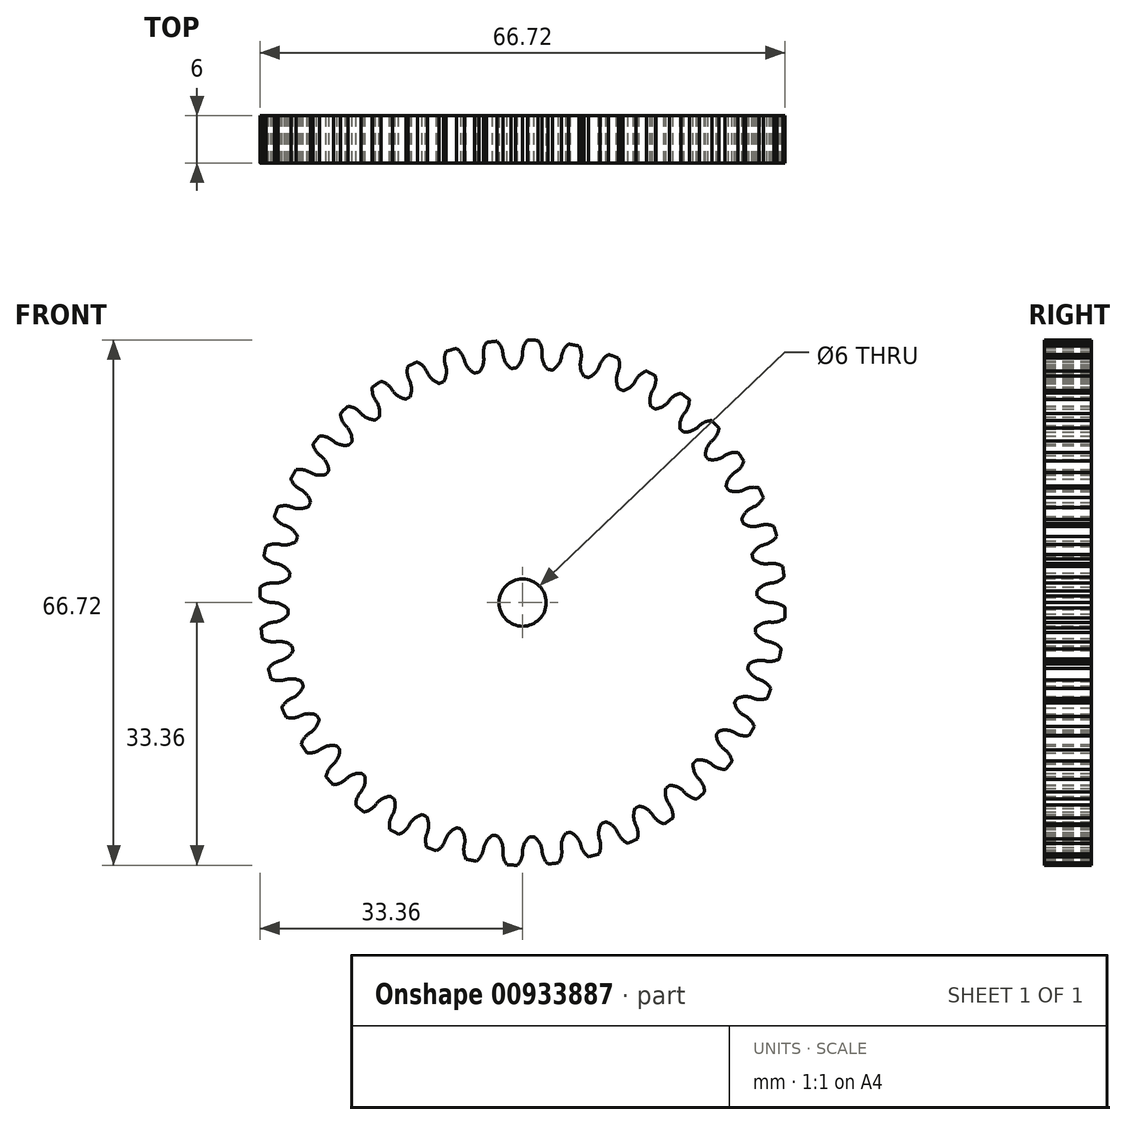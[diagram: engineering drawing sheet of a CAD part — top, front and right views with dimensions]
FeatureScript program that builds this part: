
annotation { "Feature Type Name" : "Feature", "Feature Type Description" : "" }
export const myFeature = defineFeature(function(context is Context, id is Id, definition is map)
    precondition{}
    {
        {
            var Q0;
            Q0=qCreatedBy(makeId("Front.planeOp"),FACE);
            var sketch = newSketch(context, id + "F0", { "sketchPlane" : qUnion([Q0])});
            skCircle(sketch, "E0", {"center": v(0, 0) * mm, "radius": 29.8 * mm});
            skArc(sketch, "E1", {"start": v(1.97, 33.31) * mm, "mid": v(1.31, 33.34) * mm, "end": v(0.65, 33.36) * mm});
            skArc(sketch, "E2", {"start": v(2.48, 31.49) * mm, "mid": v(2.4, 32.45) * mm, "end": v(1.97, 33.31) * mm});
            skArc(sketch, "E3", {"start": v(2.48, 31.49) * mm, "mid": v(2.65, 30.48) * mm, "end": v(3.21, 29.62) * mm});
            skArc(sketch, "E4", {"start": v(-0.88, 29.78) * mm, "mid": v(-0.2, 30.68) * mm, "end": v(0, 31.78) * mm});
            skArc(sketch, "E5.trimOffspring", {"start": v(0.65, 33.36) * mm, "mid": v(0.18, 32.63) * mm, "end": v(0, 31.78) * mm});
            skArc(sketch, "E6.1.0", {"start": v(-3.26, 33.2) * mm, "mid": v(-3.92, 33.14) * mm, "end": v(-4.58, 33.05) * mm});
            skArc(sketch, "E6.1.1", {"start": v(-4.58, 33.05) * mm, "mid": v(-4.92, 32.26) * mm, "end": v(-4.97, 31.39) * mm});
            skArc(sketch, "E6.1.2", {"start": v(-2.48, 31.49) * mm, "mid": v(-2.7, 32.43) * mm, "end": v(-3.26, 33.2) * mm});
            skArc(sketch, "E6.1.3", {"start": v(-2.48, 31.49) * mm, "mid": v(-2.15, 30.52) * mm, "end": v(-1.46, 29.76) * mm});
            skArc(sketch, "E6.1.4", {"start": v(-5.52, 29.28) * mm, "mid": v(-5, 30.27) * mm, "end": v(-4.97, 31.39) * mm});
            skArc(sketch, "E6.2.0", {"start": v(-8.42, 32.3) * mm, "mid": v(-9.06, 32.12) * mm, "end": v(-9.7, 31.93) * mm});
            skArc(sketch, "E6.2.1", {"start": v(-9.7, 31.93) * mm, "mid": v(-9.9, 31.09) * mm, "end": v(-9.82, 30.22) * mm});
            skArc(sketch, "E6.2.2", {"start": v(-7.37, 30.71) * mm, "mid": v(-7.74, 31.6) * mm, "end": v(-8.42, 32.3) * mm});
            skArc(sketch, "E6.2.3", {"start": v(-7.37, 30.71) * mm, "mid": v(-6.9, 29.8) * mm, "end": v(-6.1, 29.16) * mm});
            skArc(sketch, "E6.2.4", {"start": v(-10.04, 28.05) * mm, "mid": v(-9.68, 29.11) * mm, "end": v(-9.82, 30.22) * mm});
            skArc(sketch, "E6.3.0", {"start": v(-13.36, 30.58) * mm, "mid": v(-13.97, 30.3) * mm, "end": v(-14.57, 30.02) * mm});
            skArc(sketch, "E6.3.1", {"start": v(-14.57, 30.02) * mm, "mid": v(-14.65, 29.16) * mm, "end": v(-14.43, 28.32) * mm});
            skArc(sketch, "E6.3.2", {"start": v(-12.08, 29.18) * mm, "mid": v(-12.59, 30) * mm, "end": v(-13.36, 30.58) * mm});
            skArc(sketch, "E6.3.3", {"start": v(-12.08, 29.18) * mm, "mid": v(-11.47, 28.36) * mm, "end": v(-10.59, 27.85) * mm});
            skArc(sketch, "E6.3.4", {"start": v(-14.3, 26.14) * mm, "mid": v(-14.11, 27.24) * mm, "end": v(-14.43, 28.32) * mm});
            skArc(sketch, "E6.4.0", {"start": v(-17.98, 28.1) * mm, "mid": v(-18.54, 27.75) * mm, "end": v(-19.09, 27.37) * mm});
            skArc(sketch, "E6.4.1", {"start": v(-19.09, 27.37) * mm, "mid": v(-19.03, 26.5) * mm, "end": v(-18.68, 25.71) * mm});
            skArc(sketch, "E6.4.2", {"start": v(-16.5, 26.93) * mm, "mid": v(-17.13, 27.67) * mm, "end": v(-17.98, 28.1) * mm});
            skArc(sketch, "E6.4.3", {"start": v(-16.5, 26.93) * mm, "mid": v(-15.77, 26.21) * mm, "end": v(-14.81, 25.85) * mm});
            skArc(sketch, "E6.4.4", {"start": v(-18.21, 23.58) * mm, "mid": v(-18.2, 24.7) * mm, "end": v(-18.68, 25.71) * mm});
            skArc(sketch, "E6.5.0", {"start": v(-22.16, 24.95) * mm, "mid": v(-22.65, 24.5) * mm, "end": v(-23.13, 24.05) * mm});
            skArc(sketch, "E6.5.1", {"start": v(-23.13, 24.05) * mm, "mid": v(-22.94, 23.2) * mm, "end": v(-22.47, 22.47) * mm});
            skArc(sketch, "E6.5.2", {"start": v(-20.51, 24.02) * mm, "mid": v(-21.24, 24.65) * mm, "end": v(-22.16, 24.95) * mm});
            skArc(sketch, "E6.5.3", {"start": v(-20.51, 24.02) * mm, "mid": v(-19.68, 23.42) * mm, "end": v(-18.67, 23.22) * mm});
            skArc(sketch, "E6.5.4", {"start": v(-21.68, 20.44) * mm, "mid": v(-21.84, 21.55) * mm, "end": v(-22.47, 22.47) * mm});
            skArc(sketch, "E6.6.0", {"start": v(-25.79, 21.18) * mm, "mid": v(-26.2, 20.66) * mm, "end": v(-26.6, 20.13) * mm});
            skArc(sketch, "E6.6.1", {"start": v(-26.6, 20.13) * mm, "mid": v(-26.29, 19.33) * mm, "end": v(-25.71, 18.68) * mm});
            skArc(sketch, "E6.6.2", {"start": v(-24.02, 20.51) * mm, "mid": v(-24.84, 21.02) * mm, "end": v(-25.79, 21.18) * mm});
            skArc(sketch, "E6.6.3", {"start": v(-24.02, 20.51) * mm, "mid": v(-23.1, 20.06) * mm, "end": v(-22.08, 20) * mm});
            skArc(sketch, "E6.6.4", {"start": v(-24.6, 16.8) * mm, "mid": v(-24.94, 17.87) * mm, "end": v(-25.71, 18.68) * mm});
            skArc(sketch, "E6.7.0", {"start": v(-28.78, 16.88) * mm, "mid": v(-29.11, 16.3) * mm, "end": v(-29.43, 15.72) * mm});
            skArc(sketch, "E6.7.1", {"start": v(-29.43, 15.72) * mm, "mid": v(-28.99, 14.98) * mm, "end": v(-28.32, 14.43) * mm});
            skArc(sketch, "E6.7.2", {"start": v(-26.93, 16.5) * mm, "mid": v(-27.82, 16.88) * mm, "end": v(-28.78, 16.88) * mm});
            skArc(sketch, "E6.7.3", {"start": v(-26.93, 16.5) * mm, "mid": v(-25.95, 16.2) * mm, "end": v(-24.93, 16.3) * mm});
            skArc(sketch, "E6.7.4", {"start": v(-26.93, 12.74) * mm, "mid": v(-27.43, 13.74) * mm, "end": v(-28.32, 14.43) * mm});
            skArc(sketch, "E6.8.0", {"start": v(-31.07, 12.17) * mm, "mid": v(-31.3, 11.55) * mm, "end": v(-31.53, 10.93) * mm});
            skArc(sketch, "E6.8.1", {"start": v(-31.53, 10.93) * mm, "mid": v(-30.97, 10.26) * mm, "end": v(-30.22, 9.82) * mm});
            skArc(sketch, "E6.8.2", {"start": v(-29.18, 12.09) * mm, "mid": v(-30.12, 12.32) * mm, "end": v(-31.07, 12.17) * mm});
            skArc(sketch, "E6.8.3", {"start": v(-29.18, 12.09) * mm, "mid": v(-28.17, 11.94) * mm, "end": v(-27.18, 12.2) * mm});
            skArc(sketch, "E6.8.4", {"start": v(-28.6, 8.37) * mm, "mid": v(-29.24, 9.28) * mm, "end": v(-30.22, 9.82) * mm});
            skArc(sketch, "E6.9.0", {"start": v(-32.6, 7.16) * mm, "mid": v(-32.73, 6.51) * mm, "end": v(-32.85, 5.86) * mm});
            skArc(sketch, "E6.9.1", {"start": v(-32.85, 5.86) * mm, "mid": v(-32.2, 5.29) * mm, "end": v(-31.39, 4.97) * mm});
            skArc(sketch, "E6.9.2", {"start": v(-30.71, 7.38) * mm, "mid": v(-31.67, 7.45) * mm, "end": v(-32.6, 7.16) * mm});
            skArc(sketch, "E6.9.3", {"start": v(-30.71, 7.38) * mm, "mid": v(-29.69, 7.39) * mm, "end": v(-28.75, 7.8) * mm});
            skArc(sketch, "E6.9.4", {"start": v(-29.55, 3.8) * mm, "mid": v(-30.33, 4.6) * mm, "end": v(-31.39, 4.97) * mm});
            skArc(sketch, "E6.10.0", {"start": v(-33.31, 1.97) * mm, "mid": v(-33.34, 1.31) * mm, "end": v(-33.36, 0.65) * mm});
            skArc(sketch, "E6.10.1", {"start": v(-33.36, 0.65) * mm, "mid": v(-32.63, 0.18) * mm, "end": v(-31.78, 0) * mm});
            skArc(sketch, "E6.10.2", {"start": v(-31.49, 2.48) * mm, "mid": v(-32.45, 2.4) * mm, "end": v(-33.31, 1.97) * mm});
            skArc(sketch, "E6.10.3", {"start": v(-31.49, 2.48) * mm, "mid": v(-30.48, 2.65) * mm, "end": v(-29.62, 3.21) * mm});
            skArc(sketch, "E6.10.4", {"start": v(-29.78, -0.88) * mm, "mid": v(-30.68, -0.2) * mm, "end": v(-31.78, 0) * mm});
            skArc(sketch, "E6.11.0", {"start": v(-33.2, -3.26) * mm, "mid": v(-33.14, -3.92) * mm, "end": v(-33.05, -4.58) * mm});
            skArc(sketch, "E6.11.1", {"start": v(-33.05, -4.58) * mm, "mid": v(-32.26, -4.92) * mm, "end": v(-31.39, -4.97) * mm});
            skArc(sketch, "E6.11.2", {"start": v(-31.49, -2.48) * mm, "mid": v(-32.43, -2.7) * mm, "end": v(-33.2, -3.26) * mm});
            skArc(sketch, "E6.11.3", {"start": v(-31.49, -2.48) * mm, "mid": v(-30.52, -2.15) * mm, "end": v(-29.76, -1.46) * mm});
            skArc(sketch, "E6.11.4", {"start": v(-29.28, -5.52) * mm, "mid": v(-30.27, -5) * mm, "end": v(-31.39, -4.97) * mm});
            skArc(sketch, "E6.12.0", {"start": v(-32.3, -8.42) * mm, "mid": v(-32.12, -9.06) * mm, "end": v(-31.93, -9.7) * mm});
            skArc(sketch, "E6.12.1", {"start": v(-31.93, -9.7) * mm, "mid": v(-31.09, -9.9) * mm, "end": v(-30.22, -9.82) * mm});
            skArc(sketch, "E6.12.2", {"start": v(-30.71, -7.37) * mm, "mid": v(-31.6, -7.74) * mm, "end": v(-32.3, -8.42) * mm});
            skArc(sketch, "E6.12.3", {"start": v(-30.71, -7.37) * mm, "mid": v(-29.8, -6.9) * mm, "end": v(-29.16, -6.1) * mm});
            skArc(sketch, "E6.12.4", {"start": v(-28.05, -10.04) * mm, "mid": v(-29.11, -9.68) * mm, "end": v(-30.22, -9.82) * mm});
            skArc(sketch, "E6.13.0", {"start": v(-30.58, -13.36) * mm, "mid": v(-30.3, -13.97) * mm, "end": v(-30.02, -14.57) * mm});
            skArc(sketch, "E6.13.1", {"start": v(-30.02, -14.57) * mm, "mid": v(-29.16, -14.65) * mm, "end": v(-28.32, -14.43) * mm});
            skArc(sketch, "E6.13.2", {"start": v(-29.18, -12.08) * mm, "mid": v(-30, -12.59) * mm, "end": v(-30.58, -13.36) * mm});
            skArc(sketch, "E6.13.3", {"start": v(-29.18, -12.08) * mm, "mid": v(-28.36, -11.47) * mm, "end": v(-27.85, -10.59) * mm});
            skArc(sketch, "E6.13.4", {"start": v(-26.14, -14.3) * mm, "mid": v(-27.24, -14.11) * mm, "end": v(-28.32, -14.43) * mm});
            skArc(sketch, "E6.14.0", {"start": v(-28.1, -17.98) * mm, "mid": v(-27.75, -18.54) * mm, "end": v(-27.37, -19.09) * mm});
            skArc(sketch, "E6.14.1", {"start": v(-27.37, -19.09) * mm, "mid": v(-26.5, -19.03) * mm, "end": v(-25.71, -18.68) * mm});
            skArc(sketch, "E6.14.2", {"start": v(-26.93, -16.5) * mm, "mid": v(-27.67, -17.13) * mm, "end": v(-28.1, -17.98) * mm});
            skArc(sketch, "E6.14.3", {"start": v(-26.93, -16.5) * mm, "mid": v(-26.21, -15.77) * mm, "end": v(-25.85, -14.81) * mm});
            skArc(sketch, "E6.14.4", {"start": v(-23.58, -18.21) * mm, "mid": v(-24.7, -18.2) * mm, "end": v(-25.71, -18.68) * mm});
            skArc(sketch, "E6.15.0", {"start": v(-24.95, -22.16) * mm, "mid": v(-24.5, -22.65) * mm, "end": v(-24.05, -23.13) * mm});
            skArc(sketch, "E6.15.1", {"start": v(-24.05, -23.13) * mm, "mid": v(-23.2, -22.94) * mm, "end": v(-22.47, -22.47) * mm});
            skArc(sketch, "E6.15.2", {"start": v(-24.02, -20.51) * mm, "mid": v(-24.65, -21.24) * mm, "end": v(-24.95, -22.16) * mm});
            skArc(sketch, "E6.15.3", {"start": v(-24.02, -20.51) * mm, "mid": v(-23.42, -19.68) * mm, "end": v(-23.22, -18.67) * mm});
            skArc(sketch, "E6.15.4", {"start": v(-20.44, -21.68) * mm, "mid": v(-21.55, -21.84) * mm, "end": v(-22.47, -22.47) * mm});
            skArc(sketch, "E6.16.0", {"start": v(-21.18, -25.79) * mm, "mid": v(-20.66, -26.2) * mm, "end": v(-20.13, -26.6) * mm});
            skArc(sketch, "E6.16.1", {"start": v(-20.13, -26.6) * mm, "mid": v(-19.33, -26.29) * mm, "end": v(-18.68, -25.71) * mm});
            skArc(sketch, "E6.16.2", {"start": v(-20.51, -24.02) * mm, "mid": v(-21.02, -24.84) * mm, "end": v(-21.18, -25.79) * mm});
            skArc(sketch, "E6.16.3", {"start": v(-20.51, -24.02) * mm, "mid": v(-20.06, -23.1) * mm, "end": v(-20, -22.08) * mm});
            skArc(sketch, "E6.16.4", {"start": v(-16.8, -24.6) * mm, "mid": v(-17.87, -24.94) * mm, "end": v(-18.68, -25.71) * mm});
            skArc(sketch, "E6.17.0", {"start": v(-16.88, -28.78) * mm, "mid": v(-16.3, -29.11) * mm, "end": v(-15.72, -29.43) * mm});
            skArc(sketch, "E6.17.1", {"start": v(-15.72, -29.43) * mm, "mid": v(-14.98, -28.99) * mm, "end": v(-14.43, -28.32) * mm});
            skArc(sketch, "E6.17.2", {"start": v(-16.5, -26.93) * mm, "mid": v(-16.88, -27.82) * mm, "end": v(-16.88, -28.78) * mm});
            skArc(sketch, "E6.17.3", {"start": v(-16.5, -26.93) * mm, "mid": v(-16.2, -25.95) * mm, "end": v(-16.3, -24.93) * mm});
            skArc(sketch, "E6.17.4", {"start": v(-12.74, -26.93) * mm, "mid": v(-13.74, -27.43) * mm, "end": v(-14.43, -28.32) * mm});
            skArc(sketch, "E6.18.0", {"start": v(-12.17, -31.07) * mm, "mid": v(-11.55, -31.3) * mm, "end": v(-10.93, -31.53) * mm});
            skArc(sketch, "E6.18.1", {"start": v(-10.93, -31.53) * mm, "mid": v(-10.26, -30.97) * mm, "end": v(-9.82, -30.22) * mm});
            skArc(sketch, "E6.18.2", {"start": v(-12.09, -29.18) * mm, "mid": v(-12.32, -30.12) * mm, "end": v(-12.17, -31.07) * mm});
            skArc(sketch, "E6.18.3", {"start": v(-12.09, -29.18) * mm, "mid": v(-11.94, -28.17) * mm, "end": v(-12.2, -27.18) * mm});
            skArc(sketch, "E6.18.4", {"start": v(-8.37, -28.6) * mm, "mid": v(-9.28, -29.24) * mm, "end": v(-9.82, -30.22) * mm});
            skArc(sketch, "E6.19.0", {"start": v(-7.16, -32.6) * mm, "mid": v(-6.51, -32.73) * mm, "end": v(-5.86, -32.85) * mm});
            skArc(sketch, "E6.19.1", {"start": v(-5.86, -32.85) * mm, "mid": v(-5.29, -32.2) * mm, "end": v(-4.97, -31.39) * mm});
            skArc(sketch, "E6.19.2", {"start": v(-7.38, -30.71) * mm, "mid": v(-7.45, -31.67) * mm, "end": v(-7.16, -32.6) * mm});
            skArc(sketch, "E6.19.3", {"start": v(-7.38, -30.71) * mm, "mid": v(-7.39, -29.69) * mm, "end": v(-7.8, -28.75) * mm});
            skArc(sketch, "E6.19.4", {"start": v(-3.8, -29.55) * mm, "mid": v(-4.6, -30.33) * mm, "end": v(-4.97, -31.39) * mm});
            skArc(sketch, "E6.20.0", {"start": v(-1.97, -33.31) * mm, "mid": v(-1.31, -33.34) * mm, "end": v(-0.65, -33.36) * mm});
            skArc(sketch, "E6.20.1", {"start": v(-0.65, -33.36) * mm, "mid": v(-0.18, -32.63) * mm, "end": v(0, -31.78) * mm});
            skArc(sketch, "E6.20.2", {"start": v(-2.48, -31.49) * mm, "mid": v(-2.4, -32.45) * mm, "end": v(-1.97, -33.31) * mm});
            skArc(sketch, "E6.20.3", {"start": v(-2.48, -31.49) * mm, "mid": v(-2.65, -30.48) * mm, "end": v(-3.21, -29.62) * mm});
            skArc(sketch, "E6.20.4", {"start": v(0.88, -29.78) * mm, "mid": v(0.2, -30.68) * mm, "end": v(0, -31.78) * mm});
            skArc(sketch, "E6.21.0", {"start": v(3.26, -33.2) * mm, "mid": v(3.92, -33.14) * mm, "end": v(4.58, -33.05) * mm});
            skArc(sketch, "E6.21.1", {"start": v(4.58, -33.05) * mm, "mid": v(4.92, -32.26) * mm, "end": v(4.97, -31.39) * mm});
            skArc(sketch, "E6.21.2", {"start": v(2.48, -31.49) * mm, "mid": v(2.7, -32.43) * mm, "end": v(3.26, -33.2) * mm});
            skArc(sketch, "E6.21.3", {"start": v(2.48, -31.49) * mm, "mid": v(2.15, -30.52) * mm, "end": v(1.46, -29.76) * mm});
            skArc(sketch, "E6.21.4", {"start": v(5.52, -29.28) * mm, "mid": v(5, -30.27) * mm, "end": v(4.97, -31.39) * mm});
            skArc(sketch, "E6.22.0", {"start": v(8.42, -32.3) * mm, "mid": v(9.06, -32.12) * mm, "end": v(9.7, -31.93) * mm});
            skArc(sketch, "E6.22.1", {"start": v(9.7, -31.93) * mm, "mid": v(9.9, -31.09) * mm, "end": v(9.82, -30.22) * mm});
            skArc(sketch, "E6.22.2", {"start": v(7.37, -30.71) * mm, "mid": v(7.74, -31.6) * mm, "end": v(8.42, -32.3) * mm});
            skArc(sketch, "E6.22.3", {"start": v(7.37, -30.71) * mm, "mid": v(6.9, -29.8) * mm, "end": v(6.1, -29.16) * mm});
            skArc(sketch, "E6.22.4", {"start": v(10.04, -28.05) * mm, "mid": v(9.68, -29.11) * mm, "end": v(9.82, -30.22) * mm});
            skArc(sketch, "E6.23.0", {"start": v(13.36, -30.58) * mm, "mid": v(13.97, -30.3) * mm, "end": v(14.57, -30.02) * mm});
            skArc(sketch, "E6.23.1", {"start": v(14.57, -30.02) * mm, "mid": v(14.65, -29.16) * mm, "end": v(14.43, -28.32) * mm});
            skArc(sketch, "E6.23.2", {"start": v(12.08, -29.18) * mm, "mid": v(12.59, -30) * mm, "end": v(13.36, -30.58) * mm});
            skArc(sketch, "E6.23.3", {"start": v(12.08, -29.18) * mm, "mid": v(11.47, -28.36) * mm, "end": v(10.59, -27.85) * mm});
            skArc(sketch, "E6.23.4", {"start": v(14.3, -26.14) * mm, "mid": v(14.11, -27.24) * mm, "end": v(14.43, -28.32) * mm});
            skArc(sketch, "E6.24.0", {"start": v(17.98, -28.1) * mm, "mid": v(18.54, -27.75) * mm, "end": v(19.09, -27.37) * mm});
            skArc(sketch, "E6.24.1", {"start": v(19.09, -27.37) * mm, "mid": v(19.03, -26.5) * mm, "end": v(18.68, -25.71) * mm});
            skArc(sketch, "E6.24.2", {"start": v(16.5, -26.93) * mm, "mid": v(17.13, -27.67) * mm, "end": v(17.98, -28.1) * mm});
            skArc(sketch, "E6.24.3", {"start": v(16.5, -26.93) * mm, "mid": v(15.77, -26.21) * mm, "end": v(14.81, -25.85) * mm});
            skArc(sketch, "E6.24.4", {"start": v(18.21, -23.58) * mm, "mid": v(18.2, -24.7) * mm, "end": v(18.68, -25.71) * mm});
            skArc(sketch, "E6.25.0", {"start": v(22.16, -24.95) * mm, "mid": v(22.65, -24.5) * mm, "end": v(23.13, -24.05) * mm});
            skArc(sketch, "E6.25.1", {"start": v(23.13, -24.05) * mm, "mid": v(22.94, -23.2) * mm, "end": v(22.47, -22.47) * mm});
            skArc(sketch, "E6.25.2", {"start": v(20.51, -24.02) * mm, "mid": v(21.24, -24.65) * mm, "end": v(22.16, -24.95) * mm});
            skArc(sketch, "E6.25.3", {"start": v(20.51, -24.02) * mm, "mid": v(19.68, -23.42) * mm, "end": v(18.67, -23.22) * mm});
            skArc(sketch, "E6.25.4", {"start": v(21.68, -20.44) * mm, "mid": v(21.84, -21.55) * mm, "end": v(22.47, -22.47) * mm});
            skArc(sketch, "E6.26.0", {"start": v(25.79, -21.18) * mm, "mid": v(26.2, -20.66) * mm, "end": v(26.6, -20.13) * mm});
            skArc(sketch, "E6.26.1", {"start": v(26.6, -20.13) * mm, "mid": v(26.29, -19.33) * mm, "end": v(25.71, -18.68) * mm});
            skArc(sketch, "E6.26.2", {"start": v(24.02, -20.51) * mm, "mid": v(24.84, -21.02) * mm, "end": v(25.79, -21.18) * mm});
            skArc(sketch, "E6.26.3", {"start": v(24.02, -20.51) * mm, "mid": v(23.1, -20.06) * mm, "end": v(22.08, -20) * mm});
            skArc(sketch, "E6.26.4", {"start": v(24.6, -16.8) * mm, "mid": v(24.94, -17.87) * mm, "end": v(25.71, -18.68) * mm});
            skArc(sketch, "E6.27.0", {"start": v(28.78, -16.88) * mm, "mid": v(29.11, -16.3) * mm, "end": v(29.43, -15.72) * mm});
            skArc(sketch, "E6.27.1", {"start": v(29.43, -15.72) * mm, "mid": v(28.99, -14.98) * mm, "end": v(28.32, -14.43) * mm});
            skArc(sketch, "E6.27.2", {"start": v(26.93, -16.5) * mm, "mid": v(27.82, -16.88) * mm, "end": v(28.78, -16.88) * mm});
            skArc(sketch, "E6.27.3", {"start": v(26.93, -16.5) * mm, "mid": v(25.95, -16.2) * mm, "end": v(24.93, -16.3) * mm});
            skArc(sketch, "E6.27.4", {"start": v(26.93, -12.74) * mm, "mid": v(27.43, -13.74) * mm, "end": v(28.32, -14.43) * mm});
            skArc(sketch, "E6.28.0", {"start": v(31.07, -12.17) * mm, "mid": v(31.3, -11.55) * mm, "end": v(31.53, -10.93) * mm});
            skArc(sketch, "E6.28.1", {"start": v(31.53, -10.93) * mm, "mid": v(30.97, -10.26) * mm, "end": v(30.22, -9.82) * mm});
            skArc(sketch, "E6.28.2", {"start": v(29.18, -12.09) * mm, "mid": v(30.12, -12.32) * mm, "end": v(31.07, -12.17) * mm});
            skArc(sketch, "E6.28.3", {"start": v(29.18, -12.09) * mm, "mid": v(28.17, -11.94) * mm, "end": v(27.18, -12.2) * mm});
            skArc(sketch, "E6.28.4", {"start": v(28.6, -8.37) * mm, "mid": v(29.24, -9.28) * mm, "end": v(30.22, -9.82) * mm});
            skArc(sketch, "E6.29.0", {"start": v(32.6, -7.16) * mm, "mid": v(32.73, -6.51) * mm, "end": v(32.85, -5.86) * mm});
            skArc(sketch, "E6.29.1", {"start": v(32.85, -5.86) * mm, "mid": v(32.2, -5.29) * mm, "end": v(31.39, -4.97) * mm});
            skArc(sketch, "E6.29.2", {"start": v(30.71, -7.38) * mm, "mid": v(31.67, -7.45) * mm, "end": v(32.6, -7.16) * mm});
            skArc(sketch, "E6.29.3", {"start": v(30.71, -7.38) * mm, "mid": v(29.69, -7.39) * mm, "end": v(28.75, -7.8) * mm});
            skArc(sketch, "E6.29.4", {"start": v(29.55, -3.8) * mm, "mid": v(30.33, -4.6) * mm, "end": v(31.39, -4.97) * mm});
            skArc(sketch, "E6.30.0", {"start": v(33.31, -1.97) * mm, "mid": v(33.34, -1.31) * mm, "end": v(33.36, -0.65) * mm});
            skArc(sketch, "E6.30.1", {"start": v(33.36, -0.65) * mm, "mid": v(32.63, -0.18) * mm, "end": v(31.78, 0) * mm});
            skArc(sketch, "E6.30.2", {"start": v(31.49, -2.48) * mm, "mid": v(32.45, -2.4) * mm, "end": v(33.31, -1.97) * mm});
            skArc(sketch, "E6.30.3", {"start": v(31.49, -2.48) * mm, "mid": v(30.48, -2.65) * mm, "end": v(29.62, -3.21) * mm});
            skArc(sketch, "E6.30.4", {"start": v(29.78, 0.88) * mm, "mid": v(30.68, 0.2) * mm, "end": v(31.78, 0) * mm});
            skArc(sketch, "E6.31.0", {"start": v(33.2, 3.26) * mm, "mid": v(33.14, 3.92) * mm, "end": v(33.05, 4.58) * mm});
            skArc(sketch, "E6.31.1", {"start": v(33.05, 4.58) * mm, "mid": v(32.26, 4.92) * mm, "end": v(31.39, 4.97) * mm});
            skArc(sketch, "E6.31.2", {"start": v(31.49, 2.48) * mm, "mid": v(32.43, 2.7) * mm, "end": v(33.2, 3.26) * mm});
            skArc(sketch, "E6.31.3", {"start": v(31.49, 2.48) * mm, "mid": v(30.52, 2.15) * mm, "end": v(29.76, 1.46) * mm});
            skArc(sketch, "E6.31.4", {"start": v(29.28, 5.52) * mm, "mid": v(30.27, 5) * mm, "end": v(31.39, 4.97) * mm});
            skArc(sketch, "E6.32.0", {"start": v(32.3, 8.42) * mm, "mid": v(32.12, 9.06) * mm, "end": v(31.93, 9.7) * mm});
            skArc(sketch, "E6.32.1", {"start": v(31.93, 9.7) * mm, "mid": v(31.09, 9.9) * mm, "end": v(30.22, 9.82) * mm});
            skArc(sketch, "E6.32.2", {"start": v(30.71, 7.37) * mm, "mid": v(31.6, 7.74) * mm, "end": v(32.3, 8.42) * mm});
            skArc(sketch, "E6.32.3", {"start": v(30.71, 7.37) * mm, "mid": v(29.8, 6.9) * mm, "end": v(29.16, 6.1) * mm});
            skArc(sketch, "E6.32.4", {"start": v(28.05, 10.04) * mm, "mid": v(29.11, 9.68) * mm, "end": v(30.22, 9.82) * mm});
            skArc(sketch, "E6.33.0", {"start": v(30.58, 13.36) * mm, "mid": v(30.3, 13.97) * mm, "end": v(30.02, 14.57) * mm});
            skArc(sketch, "E6.33.1", {"start": v(30.02, 14.57) * mm, "mid": v(29.16, 14.65) * mm, "end": v(28.32, 14.43) * mm});
            skArc(sketch, "E6.33.2", {"start": v(29.18, 12.08) * mm, "mid": v(30, 12.59) * mm, "end": v(30.58, 13.36) * mm});
            skArc(sketch, "E6.33.3", {"start": v(29.18, 12.08) * mm, "mid": v(28.36, 11.47) * mm, "end": v(27.85, 10.59) * mm});
            skArc(sketch, "E6.33.4", {"start": v(26.14, 14.3) * mm, "mid": v(27.24, 14.11) * mm, "end": v(28.32, 14.43) * mm});
            skArc(sketch, "E6.34.0", {"start": v(28.1, 17.98) * mm, "mid": v(27.75, 18.54) * mm, "end": v(27.37, 19.09) * mm});
            skArc(sketch, "E6.34.1", {"start": v(27.37, 19.09) * mm, "mid": v(26.5, 19.03) * mm, "end": v(25.71, 18.68) * mm});
            skArc(sketch, "E6.34.2", {"start": v(26.93, 16.5) * mm, "mid": v(27.67, 17.13) * mm, "end": v(28.1, 17.98) * mm});
            skArc(sketch, "E6.34.3", {"start": v(26.93, 16.5) * mm, "mid": v(26.21, 15.77) * mm, "end": v(25.85, 14.81) * mm});
            skArc(sketch, "E6.34.4", {"start": v(23.58, 18.21) * mm, "mid": v(24.7, 18.2) * mm, "end": v(25.71, 18.68) * mm});
            skArc(sketch, "E6.35.0", {"start": v(24.95, 22.16) * mm, "mid": v(24.5, 22.65) * mm, "end": v(24.05, 23.13) * mm});
            skArc(sketch, "E6.35.1", {"start": v(24.05, 23.13) * mm, "mid": v(23.2, 22.94) * mm, "end": v(22.47, 22.47) * mm});
            skArc(sketch, "E6.35.2", {"start": v(24.02, 20.51) * mm, "mid": v(24.65, 21.24) * mm, "end": v(24.95, 22.16) * mm});
            skArc(sketch, "E6.35.3", {"start": v(24.02, 20.51) * mm, "mid": v(23.42, 19.68) * mm, "end": v(23.22, 18.67) * mm});
            skArc(sketch, "E6.35.4", {"start": v(20.44, 21.68) * mm, "mid": v(21.55, 21.84) * mm, "end": v(22.47, 22.47) * mm});
            skArc(sketch, "E6.36.0", {"start": v(21.18, 25.79) * mm, "mid": v(20.66, 26.2) * mm, "end": v(20.13, 26.6) * mm});
            skArc(sketch, "E6.36.1", {"start": v(20.13, 26.6) * mm, "mid": v(19.33, 26.29) * mm, "end": v(18.68, 25.71) * mm});
            skArc(sketch, "E6.36.2", {"start": v(20.51, 24.02) * mm, "mid": v(21.02, 24.84) * mm, "end": v(21.18, 25.79) * mm});
            skArc(sketch, "E6.36.3", {"start": v(20.51, 24.02) * mm, "mid": v(20.06, 23.1) * mm, "end": v(20, 22.08) * mm});
            skArc(sketch, "E6.36.4", {"start": v(16.8, 24.6) * mm, "mid": v(17.87, 24.94) * mm, "end": v(18.68, 25.71) * mm});
            skArc(sketch, "E6.37.0", {"start": v(16.88, 28.78) * mm, "mid": v(16.3, 29.11) * mm, "end": v(15.72, 29.43) * mm});
            skArc(sketch, "E6.37.1", {"start": v(15.72, 29.43) * mm, "mid": v(14.98, 28.99) * mm, "end": v(14.43, 28.32) * mm});
            skArc(sketch, "E6.37.2", {"start": v(16.5, 26.93) * mm, "mid": v(16.88, 27.82) * mm, "end": v(16.88, 28.78) * mm});
            skArc(sketch, "E6.37.3", {"start": v(16.5, 26.93) * mm, "mid": v(16.2, 25.95) * mm, "end": v(16.3, 24.93) * mm});
            skArc(sketch, "E6.37.4", {"start": v(12.74, 26.93) * mm, "mid": v(13.74, 27.43) * mm, "end": v(14.43, 28.32) * mm});
            skArc(sketch, "E6.38.0", {"start": v(12.17, 31.07) * mm, "mid": v(11.55, 31.3) * mm, "end": v(10.93, 31.53) * mm});
            skArc(sketch, "E6.38.1", {"start": v(10.93, 31.53) * mm, "mid": v(10.26, 30.97) * mm, "end": v(9.82, 30.22) * mm});
            skArc(sketch, "E6.38.2", {"start": v(12.09, 29.18) * mm, "mid": v(12.32, 30.12) * mm, "end": v(12.17, 31.07) * mm});
            skArc(sketch, "E6.38.3", {"start": v(12.09, 29.18) * mm, "mid": v(11.94, 28.17) * mm, "end": v(12.2, 27.18) * mm});
            skArc(sketch, "E6.38.4", {"start": v(8.37, 28.6) * mm, "mid": v(9.28, 29.24) * mm, "end": v(9.82, 30.22) * mm});
            skArc(sketch, "E6.39.0", {"start": v(7.16, 32.6) * mm, "mid": v(6.51, 32.73) * mm, "end": v(5.86, 32.85) * mm});
            skArc(sketch, "E6.39.1", {"start": v(5.86, 32.85) * mm, "mid": v(5.29, 32.2) * mm, "end": v(4.97, 31.39) * mm});
            skArc(sketch, "E6.39.2", {"start": v(7.38, 30.71) * mm, "mid": v(7.45, 31.67) * mm, "end": v(7.16, 32.6) * mm});
            skArc(sketch, "E6.39.3", {"start": v(7.38, 30.71) * mm, "mid": v(7.39, 29.69) * mm, "end": v(7.8, 28.75) * mm});
            skArc(sketch, "E6.39.4", {"start": v(3.8, 29.55) * mm, "mid": v(4.6, 30.33) * mm, "end": v(4.97, 31.39) * mm});
            skSolve(sketch);
        }
        {
            var Q0;
            Q0 = qSketchRegion(id + "F0", true);
            extrude(context, id + "F1", {"entities" : qUnion([Q0]), "depth" : 6 * mm, "offsetDistance" : 25 * mm});
        }
        {
            var Q0;
            Q0=makeQuery(id+"F1.opExtrude","CAP_FACE",FACE,{"disambiguationData":[OSD([sQuery(id+"F0.wireOp",EDGE,"E0"),sQuery(id+"F0.wireOp",EDGE,"E1"),sQuery(id+"F0.wireOp",EDGE,"E2"),sQuery(id+"F0.wireOp",EDGE,"E3"),sQuery(id+"F0.wireOp",EDGE,"E4"),sQuery(id+"F0.wireOp",EDGE,"E5.trimOffspring"),sQuery(id+"F0.wireOp",EDGE,"E6.1.0"),sQuery(id+"F0.wireOp",EDGE,"E6.1.1"),sQuery(id+"F0.wireOp",EDGE,"E6.1.2"),sQuery(id+"F0.wireOp",EDGE,"E6.1.3"),sQuery(id+"F0.wireOp",EDGE,"E6.1.4"),sQuery(id+"F0.wireOp",EDGE,"E6.2.0"),sQuery(id+"F0.wireOp",EDGE,"E6.2.1"),sQuery(id+"F0.wireOp",EDGE,"E6.2.2"),sQuery(id+"F0.wireOp",EDGE,"E6.2.3"),sQuery(id+"F0.wireOp",EDGE,"E6.2.4"),sQuery(id+"F0.wireOp",EDGE,"E6.3.0"),sQuery(id+"F0.wireOp",EDGE,"E6.3.1"),sQuery(id+"F0.wireOp",EDGE,"E6.3.2"),sQuery(id+"F0.wireOp",EDGE,"E6.3.3"),sQuery(id+"F0.wireOp",EDGE,"E6.3.4"),sQuery(id+"F0.wireOp",EDGE,"E6.4.0"),sQuery(id+"F0.wireOp",EDGE,"E6.4.1"),sQuery(id+"F0.wireOp",EDGE,"E6.4.2"),sQuery(id+"F0.wireOp",EDGE,"E6.4.3"),sQuery(id+"F0.wireOp",EDGE,"E6.4.4"),sQuery(id+"F0.wireOp",EDGE,"E6.5.0"),sQuery(id+"F0.wireOp",EDGE,"E6.5.1"),sQuery(id+"F0.wireOp",EDGE,"E6.5.2"),sQuery(id+"F0.wireOp",EDGE,"E6.5.3"),sQuery(id+"F0.wireOp",EDGE,"E6.5.4"),sQuery(id+"F0.wireOp",EDGE,"E6.6.0"),sQuery(id+"F0.wireOp",EDGE,"E6.6.1"),sQuery(id+"F0.wireOp",EDGE,"E6.6.2"),sQuery(id+"F0.wireOp",EDGE,"E6.6.3"),sQuery(id+"F0.wireOp",EDGE,"E6.6.4"),sQuery(id+"F0.wireOp",EDGE,"E6.7.0"),sQuery(id+"F0.wireOp",EDGE,"E6.7.1"),sQuery(id+"F0.wireOp",EDGE,"E6.7.2"),sQuery(id+"F0.wireOp",EDGE,"E6.7.3"),sQuery(id+"F0.wireOp",EDGE,"E6.7.4"),sQuery(id+"F0.wireOp",EDGE,"E6.8.0"),sQuery(id+"F0.wireOp",EDGE,"E6.8.1"),sQuery(id+"F0.wireOp",EDGE,"E6.8.2"),sQuery(id+"F0.wireOp",EDGE,"E6.8.3"),sQuery(id+"F0.wireOp",EDGE,"E6.8.4"),sQuery(id+"F0.wireOp",EDGE,"E6.9.0"),sQuery(id+"F0.wireOp",EDGE,"E6.9.1"),sQuery(id+"F0.wireOp",EDGE,"E6.9.2"),sQuery(id+"F0.wireOp",EDGE,"E6.9.3"),sQuery(id+"F0.wireOp",EDGE,"E6.9.4"),sQuery(id+"F0.wireOp",EDGE,"E6.10.0"),sQuery(id+"F0.wireOp",EDGE,"E6.10.1"),sQuery(id+"F0.wireOp",EDGE,"E6.10.2"),sQuery(id+"F0.wireOp",EDGE,"E6.10.3"),sQuery(id+"F0.wireOp",EDGE,"E6.10.4"),sQuery(id+"F0.wireOp",EDGE,"E6.11.0"),sQuery(id+"F0.wireOp",EDGE,"E6.11.1"),sQuery(id+"F0.wireOp",EDGE,"E6.11.2"),sQuery(id+"F0.wireOp",EDGE,"E6.11.3"),sQuery(id+"F0.wireOp",EDGE,"E6.11.4"),sQuery(id+"F0.wireOp",EDGE,"E6.12.0"),sQuery(id+"F0.wireOp",EDGE,"E6.12.1"),sQuery(id+"F0.wireOp",EDGE,"E6.12.2"),sQuery(id+"F0.wireOp",EDGE,"E6.12.3"),sQuery(id+"F0.wireOp",EDGE,"E6.12.4"),sQuery(id+"F0.wireOp",EDGE,"E6.13.0"),sQuery(id+"F0.wireOp",EDGE,"E6.13.1"),sQuery(id+"F0.wireOp",EDGE,"E6.13.2"),sQuery(id+"F0.wireOp",EDGE,"E6.13.3"),sQuery(id+"F0.wireOp",EDGE,"E6.13.4"),sQuery(id+"F0.wireOp",EDGE,"E6.14.0"),sQuery(id+"F0.wireOp",EDGE,"E6.14.1"),sQuery(id+"F0.wireOp",EDGE,"E6.14.2"),sQuery(id+"F0.wireOp",EDGE,"E6.14.3"),sQuery(id+"F0.wireOp",EDGE,"E6.14.4"),sQuery(id+"F0.wireOp",EDGE,"E6.15.0"),sQuery(id+"F0.wireOp",EDGE,"E6.15.1"),sQuery(id+"F0.wireOp",EDGE,"E6.15.2"),sQuery(id+"F0.wireOp",EDGE,"E6.15.3"),sQuery(id+"F0.wireOp",EDGE,"E6.15.4"),sQuery(id+"F0.wireOp",EDGE,"E6.16.0"),sQuery(id+"F0.wireOp",EDGE,"E6.16.1"),sQuery(id+"F0.wireOp",EDGE,"E6.16.2"),sQuery(id+"F0.wireOp",EDGE,"E6.16.3"),sQuery(id+"F0.wireOp",EDGE,"E6.16.4"),sQuery(id+"F0.wireOp",EDGE,"E6.17.0"),sQuery(id+"F0.wireOp",EDGE,"E6.17.1"),sQuery(id+"F0.wireOp",EDGE,"E6.17.2"),sQuery(id+"F0.wireOp",EDGE,"E6.17.3"),sQuery(id+"F0.wireOp",EDGE,"E6.17.4"),sQuery(id+"F0.wireOp",EDGE,"E6.18.0"),sQuery(id+"F0.wireOp",EDGE,"E6.18.1"),sQuery(id+"F0.wireOp",EDGE,"E6.18.2"),sQuery(id+"F0.wireOp",EDGE,"E6.18.3"),sQuery(id+"F0.wireOp",EDGE,"E6.18.4"),sQuery(id+"F0.wireOp",EDGE,"E6.19.0"),sQuery(id+"F0.wireOp",EDGE,"E6.19.1"),sQuery(id+"F0.wireOp",EDGE,"E6.19.2"),sQuery(id+"F0.wireOp",EDGE,"E6.19.3"),sQuery(id+"F0.wireOp",EDGE,"E6.19.4"),sQuery(id+"F0.wireOp",EDGE,"E6.20.0"),sQuery(id+"F0.wireOp",EDGE,"E6.20.1"),sQuery(id+"F0.wireOp",EDGE,"E6.20.2"),sQuery(id+"F0.wireOp",EDGE,"E6.20.3"),sQuery(id+"F0.wireOp",EDGE,"E6.20.4"),sQuery(id+"F0.wireOp",EDGE,"E6.21.0"),sQuery(id+"F0.wireOp",EDGE,"E6.21.1"),sQuery(id+"F0.wireOp",EDGE,"E6.21.2"),sQuery(id+"F0.wireOp",EDGE,"E6.21.3"),sQuery(id+"F0.wireOp",EDGE,"E6.21.4"),sQuery(id+"F0.wireOp",EDGE,"E6.22.0"),sQuery(id+"F0.wireOp",EDGE,"E6.22.1"),sQuery(id+"F0.wireOp",EDGE,"E6.22.2"),sQuery(id+"F0.wireOp",EDGE,"E6.22.3"),sQuery(id+"F0.wireOp",EDGE,"E6.22.4"),sQuery(id+"F0.wireOp",EDGE,"E6.23.0"),sQuery(id+"F0.wireOp",EDGE,"E6.23.1"),sQuery(id+"F0.wireOp",EDGE,"E6.23.2"),sQuery(id+"F0.wireOp",EDGE,"E6.23.3"),sQuery(id+"F0.wireOp",EDGE,"E6.23.4"),sQuery(id+"F0.wireOp",EDGE,"E6.24.0"),sQuery(id+"F0.wireOp",EDGE,"E6.24.1"),sQuery(id+"F0.wireOp",EDGE,"E6.24.2"),sQuery(id+"F0.wireOp",EDGE,"E6.24.3"),sQuery(id+"F0.wireOp",EDGE,"E6.24.4"),sQuery(id+"F0.wireOp",EDGE,"E6.25.0"),sQuery(id+"F0.wireOp",EDGE,"E6.25.1"),sQuery(id+"F0.wireOp",EDGE,"E6.25.2"),sQuery(id+"F0.wireOp",EDGE,"E6.25.3"),sQuery(id+"F0.wireOp",EDGE,"E6.25.4"),sQuery(id+"F0.wireOp",EDGE,"E6.26.0"),sQuery(id+"F0.wireOp",EDGE,"E6.26.1"),sQuery(id+"F0.wireOp",EDGE,"E6.26.2"),sQuery(id+"F0.wireOp",EDGE,"E6.26.3"),sQuery(id+"F0.wireOp",EDGE,"E6.26.4"),sQuery(id+"F0.wireOp",EDGE,"E6.27.0"),sQuery(id+"F0.wireOp",EDGE,"E6.27.1"),sQuery(id+"F0.wireOp",EDGE,"E6.27.2"),sQuery(id+"F0.wireOp",EDGE,"E6.27.3"),sQuery(id+"F0.wireOp",EDGE,"E6.27.4"),sQuery(id+"F0.wireOp",EDGE,"E6.28.0"),sQuery(id+"F0.wireOp",EDGE,"E6.28.1"),sQuery(id+"F0.wireOp",EDGE,"E6.28.2"),sQuery(id+"F0.wireOp",EDGE,"E6.28.3"),sQuery(id+"F0.wireOp",EDGE,"E6.28.4"),sQuery(id+"F0.wireOp",EDGE,"E6.29.0"),sQuery(id+"F0.wireOp",EDGE,"E6.29.1"),sQuery(id+"F0.wireOp",EDGE,"E6.29.2"),sQuery(id+"F0.wireOp",EDGE,"E6.29.3"),sQuery(id+"F0.wireOp",EDGE,"E6.29.4"),sQuery(id+"F0.wireOp",EDGE,"E6.30.0"),sQuery(id+"F0.wireOp",EDGE,"E6.30.1"),sQuery(id+"F0.wireOp",EDGE,"E6.30.2"),sQuery(id+"F0.wireOp",EDGE,"E6.30.3"),sQuery(id+"F0.wireOp",EDGE,"E6.30.4"),sQuery(id+"F0.wireOp",EDGE,"E6.31.0"),sQuery(id+"F0.wireOp",EDGE,"E6.31.1"),sQuery(id+"F0.wireOp",EDGE,"E6.31.2"),sQuery(id+"F0.wireOp",EDGE,"E6.31.3"),sQuery(id+"F0.wireOp",EDGE,"E6.31.4"),sQuery(id+"F0.wireOp",EDGE,"E6.32.0"),sQuery(id+"F0.wireOp",EDGE,"E6.32.1"),sQuery(id+"F0.wireOp",EDGE,"E6.32.2"),sQuery(id+"F0.wireOp",EDGE,"E6.32.3"),sQuery(id+"F0.wireOp",EDGE,"E6.32.4"),sQuery(id+"F0.wireOp",EDGE,"E6.33.0"),sQuery(id+"F0.wireOp",EDGE,"E6.33.1"),sQuery(id+"F0.wireOp",EDGE,"E6.33.2"),sQuery(id+"F0.wireOp",EDGE,"E6.33.3"),sQuery(id+"F0.wireOp",EDGE,"E6.33.4"),sQuery(id+"F0.wireOp",EDGE,"E6.34.0"),sQuery(id+"F0.wireOp",EDGE,"E6.34.1"),sQuery(id+"F0.wireOp",EDGE,"E6.34.2"),sQuery(id+"F0.wireOp",EDGE,"E6.34.3"),sQuery(id+"F0.wireOp",EDGE,"E6.34.4"),sQuery(id+"F0.wireOp",EDGE,"E6.35.0"),sQuery(id+"F0.wireOp",EDGE,"E6.35.1"),sQuery(id+"F0.wireOp",EDGE,"E6.35.2"),sQuery(id+"F0.wireOp",EDGE,"E6.35.3"),sQuery(id+"F0.wireOp",EDGE,"E6.35.4"),sQuery(id+"F0.wireOp",EDGE,"E6.36.0"),sQuery(id+"F0.wireOp",EDGE,"E6.36.1"),sQuery(id+"F0.wireOp",EDGE,"E6.36.2"),sQuery(id+"F0.wireOp",EDGE,"E6.36.3"),sQuery(id+"F0.wireOp",EDGE,"E6.36.4"),sQuery(id+"F0.wireOp",EDGE,"E6.37.0"),sQuery(id+"F0.wireOp",EDGE,"E6.37.1"),sQuery(id+"F0.wireOp",EDGE,"E6.37.2"),sQuery(id+"F0.wireOp",EDGE,"E6.37.3"),sQuery(id+"F0.wireOp",EDGE,"E6.37.4"),sQuery(id+"F0.wireOp",EDGE,"E6.38.0"),sQuery(id+"F0.wireOp",EDGE,"E6.38.1"),sQuery(id+"F0.wireOp",EDGE,"E6.38.2"),sQuery(id+"F0.wireOp",EDGE,"E6.38.3"),sQuery(id+"F0.wireOp",EDGE,"E6.38.4"),sQuery(id+"F0.wireOp",EDGE,"E6.39.0"),sQuery(id+"F0.wireOp",EDGE,"E6.39.1"),sQuery(id+"F0.wireOp",EDGE,"E6.39.2"),sQuery(id+"F0.wireOp",EDGE,"E6.39.3"),sQuery(id+"F0.wireOp",EDGE,"E6.39.4")])],"isStart":false});
            var sketch = newSketch(context, id + "F2", { "sketchPlane" : qUnion([Q0])});
            skCircle(sketch, "E7", {"center": v(0, 0) * mm, "radius": 3 * mm});
            skSolve(sketch);
        }
        {
            var Q0;
            Q0 = qSketchRegion(id + "F2", true);
            extrude(context, id + "F3", {"entities" : qUnion([Q0]), "operationType" : NewBodyOperationType.REMOVE, "endBound" : BoundingType.THROUGH_ALL, "oppositeDirection" : true, "depth" : 25 * mm, "offsetDistance" : 25 * mm});
        }
    });
